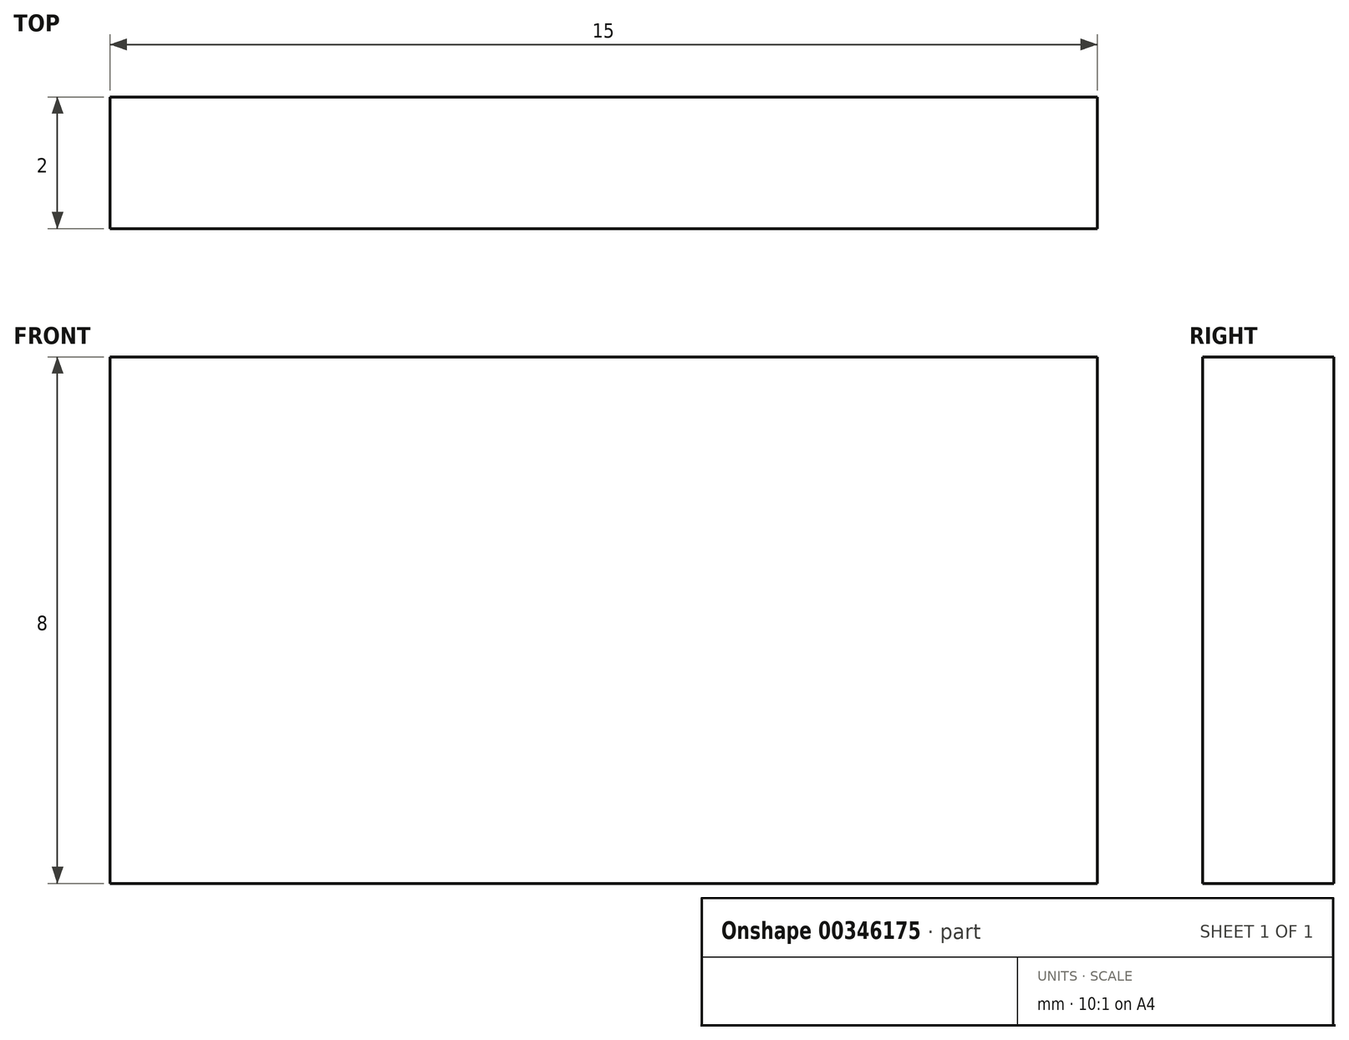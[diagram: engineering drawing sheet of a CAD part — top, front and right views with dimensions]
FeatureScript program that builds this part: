
annotation { "Feature Type Name" : "Feature", "Feature Type Description" : "" }
export const myFeature = defineFeature(function(context is Context, id is Id, definition is map)
    precondition{}
    {
        {
            var Q0;
            Q0=qCreatedBy(makeId("Top.planeOp"),FACE);
            var sketch = newSketch(context, id + "F0", { "sketchPlane" : qUnion([Q0])});
            skLineSegment(sketch, "E0.bottom", {"start": v(0, 0) * mm, "end": v(15, 0) * mm});
            skLineSegment(sketch, "E0.top", {"start": v(0, -2) * mm, "end": v(15, -2) * mm});
            skLineSegment(sketch, "E0.left", {"start": v(0, 0) * mm, "end": v(0, -2) * mm});
            skLineSegment(sketch, "E0.right", {"start": v(15, 0) * mm, "end": v(15, -2) * mm});
            skLineSegment(sketch, "E1.bottom", {"start": v(15, 0) * mm, "end": v(13, 0) * mm});
            skLineSegment(sketch, "E1.top", {"start": v(15, 10) * mm, "end": v(13, 10) * mm});
            skLineSegment(sketch, "E1.left", {"start": v(15, 0) * mm, "end": v(15, 10) * mm});
            skLineSegment(sketch, "E1.right", {"start": v(13, 0) * mm, "end": v(13, 10) * mm});
            skSolve(sketch);
        }
        {
            var Q0;
            Q0=makeQuery(id+"F0.imprint","IMPRINT",FACE,{"disambiguationData":[TD([[makeQuery(id+"F0.imprint","IMPRINT",EDGE,{"derivedFrom":sQuery(id+"F0.wireOp",EDGE,"E0.bottom")}),-1.0]])]});
            var Q1;
            Q1=makeQuery(id+"F0.imprint","IMPRINT",FACE,{"disambiguationData":[TD([[makeQuery(id+"F0.imprint","IMPRINT",EDGE,{"derivedFrom":sQuery(id+"F0.wireOp",EDGE,"E1.bottom")}),-1.0]])]});
            extrude(context, id + "F1", {"entities" : qUnion([Q0, Q1]), "depth" : 8 * mm});
        }
    });
